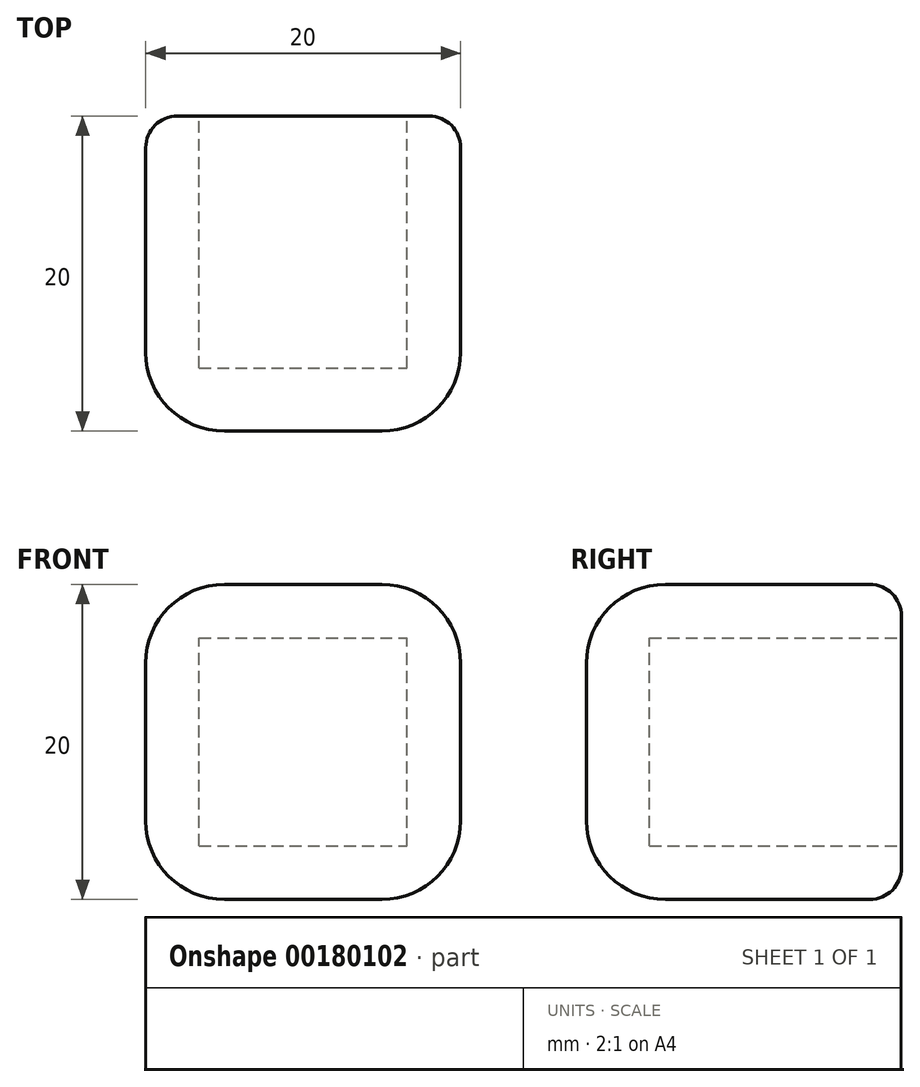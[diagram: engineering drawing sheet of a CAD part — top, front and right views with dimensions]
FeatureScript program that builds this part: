
annotation { "Feature Type Name" : "Feature", "Feature Type Description" : "" }
export const myFeature = defineFeature(function(context is Context, id is Id, definition is map)
    precondition{}
    {
        {
            var Q0;
            Q0=qCreatedBy(makeId("Front.planeOp"),FACE);
            var sketch = newSketch(context, id + "F0", { "sketchPlane" : qUnion([Q0])});
            skLineSegment(sketch, "E0.bottom", {"start": v(0, 0) * mm, "end": v(20, 0) * mm});
            skLineSegment(sketch, "E0.top", {"start": v(0, 20) * mm, "end": v(20, 20) * mm});
            skLineSegment(sketch, "E0.left", {"start": v(0, 0) * mm, "end": v(0, 20) * mm});
            skLineSegment(sketch, "E0.right", {"start": v(20, 0) * mm, "end": v(20, 20) * mm});
            skSolve(sketch);
        }
        {
            var Q0;
            Q0=qSketchRegion(id+"F0",true);
            extrude(context, id + "F1", {"entities" : qUnion([Q0]), "depth" : 20 * mm});
        }
        {
            var Q0;
            Q0=makeQuery(id+"F1.opExtrude","CAP_FACE",FACE,{"disambiguationData":[OSD([sQuery(id+"F0.wireOp",EDGE,"E0.bottom"),sQuery(id+"F0.wireOp",EDGE,"E0.top"),sQuery(id+"F0.wireOp",EDGE,"E0.left"),sQuery(id+"F0.wireOp",EDGE,"E0.right")])],"isStart":true});
            var sketch = newSketch(context, id + "F2", { "sketchPlane" : qUnion([Q0])});
            skPoint(sketch, "E1", {"position": v(-3.4, 3.4) * mm});
            skLineSegment(sketch, "E2.bottom", {"start": v(-3.4, 3.4) * mm, "end": v(-16.6, 3.4) * mm});
            skLineSegment(sketch, "E2.top", {"start": v(-3.4, 16.6) * mm, "end": v(-16.6, 16.6) * mm});
            skLineSegment(sketch, "E2.left", {"start": v(-3.4, 3.4) * mm, "end": v(-3.4, 16.6) * mm});
            skLineSegment(sketch, "E2.right", {"start": v(-16.6, 3.4) * mm, "end": v(-16.6, 16.6) * mm});
            skSolve(sketch);
        }
        {
            var Q0;
            Q0=makeQuery(id+"F2.imprint","IMPRINT",FACE,{"disambiguationData":[TD([[makeQuery(id+"F2.imprint","IMPRINT",EDGE,{"derivedFrom":sQuery(id+"F2.wireOp",EDGE,"E2.bottom")}),-1.0]])]});
            extrude(context, id + "F3", {"entities" : qUnion([Q0]), "operationType" : NewBodyOperationType.REMOVE, "oppositeDirection" : true, "depth" : 16 * mm});
        }
        {
            var Q0;
            Q0=makeQuery(id+"F1.opExtrude","CAP_FACE",FACE,{"disambiguationData":[OSD([sQuery(id+"F0.wireOp",EDGE,"E0.bottom"),sQuery(id+"F0.wireOp",EDGE,"E0.top"),sQuery(id+"F0.wireOp",EDGE,"E0.left"),sQuery(id+"F0.wireOp",EDGE,"E0.right")])],"isStart":false});
            var Q1;
            Q1=makeQuery(id+"F1.opExtrude","SWEPT_EDGE",EDGE,{"disambiguationData":[OSD([sQuery(id+"F0.wireOp",EDGE,"E0.top"),sQuery(id+"F0.wireOp",EDGE,"E0.right")])]});
            var Q2;
            Q2=makeQuery(id+"F1.opExtrude","SWEPT_EDGE",EDGE,{"disambiguationData":[OSD([sQuery(id+"F0.wireOp",EDGE,"E0.top"),sQuery(id+"F0.wireOp",EDGE,"E0.left")])]});
            var Q3;
            Q3=makeQuery(id+"F1.opExtrude","SWEPT_EDGE",EDGE,{"disambiguationData":[OSD([sQuery(id+"F0.wireOp",EDGE,"E0.bottom"),sQuery(id+"F0.wireOp",EDGE,"E0.right")])]});
            var Q4;
            Q4=makeQuery(id+"F1.opExtrude","SWEPT_EDGE",EDGE,{"disambiguationData":[OSD([sQuery(id+"F0.wireOp",EDGE,"E0.bottom"),sQuery(id+"F0.wireOp",EDGE,"E0.left")])]});
            fillet(context, id + "F4", {"entities" : qUnion([Q0, Q1, Q2, Q3, Q4]), "radius" : 5 * mm, "tangentPropagation" : true, "allowEdgeOverflow" : false});
        }
        {
            var Q0;
            {var subQ0=sQuery(id+"F0.wireOp",EDGE,"E0.right");var subQ1=sQuery(id+"F0.wireOp",EDGE,"E0.bottom");Q0=makeQuery(id+"F4.opFillet","BLEND_EDGE",EDGE,{"blendedFrom":[makeQuery(id+"F1.opExtrude","SWEPT_EDGE",EDGE,{"disambiguationData":[OSD([subQ1,subQ0])]}),makeQuery(id+"F1.opExtrude","CAP_FACE",FACE,{"disambiguationData":[OSD([subQ1,sQuery(id+"F0.wireOp",EDGE,"E0.top"),sQuery(id+"F0.wireOp",EDGE,"E0.left"),subQ0])],"isStart":true})],"blendedInto":[makeQuery(id+"F1.opExtrude","CAP_FACE",FACE,{"disambiguationData":[OSD([subQ1,sQuery(id+"F0.wireOp",EDGE,"E0.top"),sQuery(id+"F0.wireOp",EDGE,"E0.left"),subQ0])],"isStart":true})]});}
            var Q1;
            Q1=makeQuery(id+"F1.opExtrude","CAP_EDGE",EDGE,{"disambiguationData":[OSD([sQuery(id+"F0.wireOp",EDGE,"E0.right")])],"isStart":true});
            var Q2;
            {var subQ0=sQuery(id+"F0.wireOp",EDGE,"E0.right");var subQ1=sQuery(id+"F0.wireOp",EDGE,"E0.top");Q2=makeQuery(id+"F4.opFillet","BLEND_EDGE",EDGE,{"blendedFrom":[makeQuery(id+"F1.opExtrude","SWEPT_EDGE",EDGE,{"disambiguationData":[OSD([subQ1,subQ0])]}),makeQuery(id+"F1.opExtrude","CAP_FACE",FACE,{"disambiguationData":[OSD([sQuery(id+"F0.wireOp",EDGE,"E0.bottom"),subQ1,sQuery(id+"F0.wireOp",EDGE,"E0.left"),subQ0])],"isStart":true})],"blendedInto":[makeQuery(id+"F1.opExtrude","CAP_FACE",FACE,{"disambiguationData":[OSD([sQuery(id+"F0.wireOp",EDGE,"E0.bottom"),subQ1,sQuery(id+"F0.wireOp",EDGE,"E0.left"),subQ0])],"isStart":true})]});}
            var Q3;
            Q3=makeQuery(id+"F1.opExtrude","CAP_EDGE",EDGE,{"disambiguationData":[OSD([sQuery(id+"F0.wireOp",EDGE,"E0.top")])],"isStart":true});
            var Q4;
            {var subQ0=sQuery(id+"F0.wireOp",EDGE,"E0.left");var subQ1=sQuery(id+"F0.wireOp",EDGE,"E0.top");Q4=makeQuery(id+"F4.opFillet","BLEND_EDGE",EDGE,{"blendedFrom":[makeQuery(id+"F1.opExtrude","SWEPT_EDGE",EDGE,{"disambiguationData":[OSD([subQ1,subQ0])]}),makeQuery(id+"F1.opExtrude","CAP_FACE",FACE,{"disambiguationData":[OSD([sQuery(id+"F0.wireOp",EDGE,"E0.bottom"),subQ1,subQ0,sQuery(id+"F0.wireOp",EDGE,"E0.right")])],"isStart":true})],"blendedInto":[makeQuery(id+"F1.opExtrude","CAP_FACE",FACE,{"disambiguationData":[OSD([sQuery(id+"F0.wireOp",EDGE,"E0.bottom"),subQ1,subQ0,sQuery(id+"F0.wireOp",EDGE,"E0.right")])],"isStart":true})]});}
            var Q5;
            Q5=makeQuery(id+"F1.opExtrude","CAP_EDGE",EDGE,{"disambiguationData":[OSD([sQuery(id+"F0.wireOp",EDGE,"E0.left")])],"isStart":true});
            var Q6;
            {var subQ0=sQuery(id+"F0.wireOp",EDGE,"E0.left");var subQ1=sQuery(id+"F0.wireOp",EDGE,"E0.bottom");Q6=makeQuery(id+"F4.opFillet","BLEND_EDGE",EDGE,{"blendedFrom":[makeQuery(id+"F1.opExtrude","SWEPT_EDGE",EDGE,{"disambiguationData":[OSD([subQ1,subQ0])]}),makeQuery(id+"F1.opExtrude","CAP_FACE",FACE,{"disambiguationData":[OSD([subQ1,sQuery(id+"F0.wireOp",EDGE,"E0.top"),subQ0,sQuery(id+"F0.wireOp",EDGE,"E0.right")])],"isStart":true})],"blendedInto":[makeQuery(id+"F1.opExtrude","CAP_FACE",FACE,{"disambiguationData":[OSD([subQ1,sQuery(id+"F0.wireOp",EDGE,"E0.top"),subQ0,sQuery(id+"F0.wireOp",EDGE,"E0.right")])],"isStart":true})]});}
            var Q7;
            Q7=makeQuery(id+"F1.opExtrude","CAP_EDGE",EDGE,{"disambiguationData":[OSD([sQuery(id+"F0.wireOp",EDGE,"E0.bottom")])],"isStart":true});
            fillet(context, id + "F5", {"entities" : qUnion([Q0, Q1, Q2, Q3, Q4, Q5, Q6, Q7]), "radius" : 2 * mm, "tangentPropagation" : true, "allowEdgeOverflow" : false});
        }
    });
